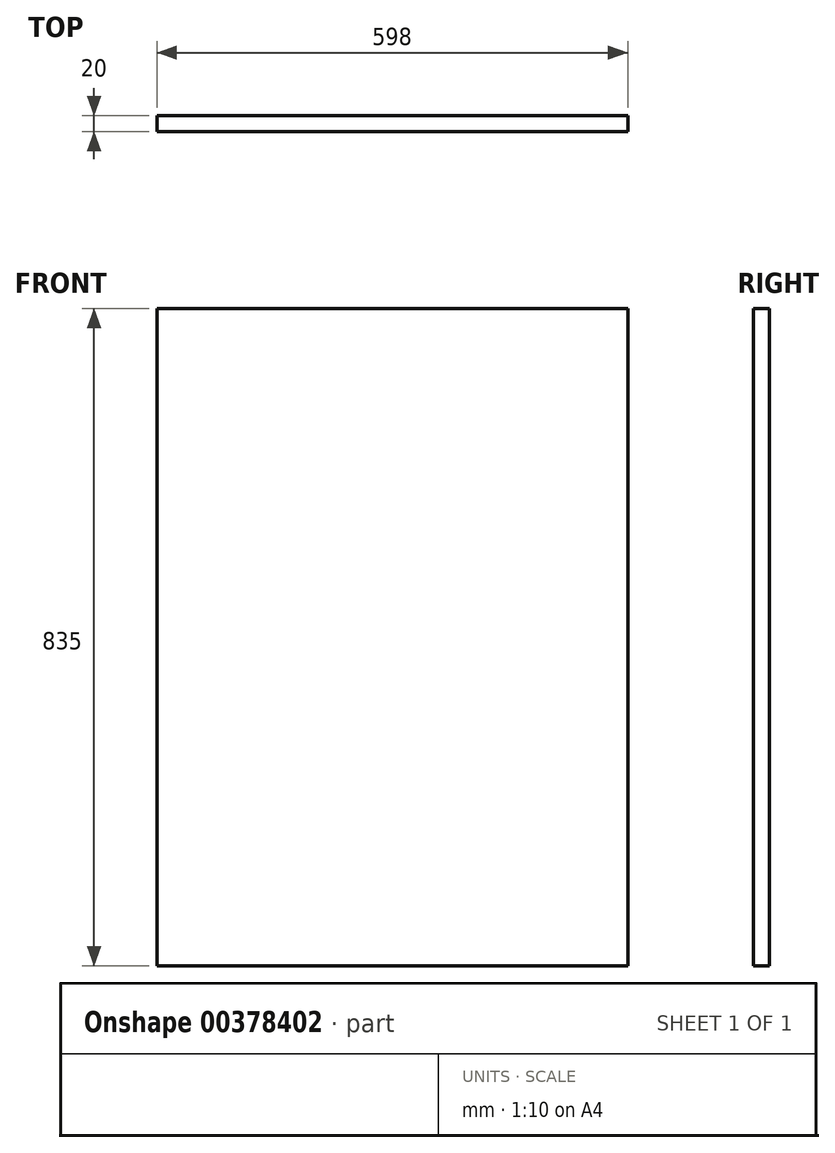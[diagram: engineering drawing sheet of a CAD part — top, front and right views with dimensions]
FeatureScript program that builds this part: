
annotation { "Feature Type Name" : "Feature", "Feature Type Description" : "" }
export const myFeature = defineFeature(function(context is Context, id is Id, definition is map)
    precondition{}
    {
        {
            var Q0;
            Q0=qCreatedBy(makeId("Front.planeOp"),FACE);
            var sketch = newSketch(context, id + "F0", { "sketchPlane" : qUnion([Q0])});
            skLineSegment(sketch, "E0.bottom", {"start": v(299, 417.5) * mm, "end": v(-299, 417.5) * mm});
            skLineSegment(sketch, "E0.top", {"start": v(299, -417.5) * mm, "end": v(-299, -417.5) * mm});
            skLineSegment(sketch, "E0.left", {"start": v(299, 417.5) * mm, "end": v(299, -417.5) * mm});
            skLineSegment(sketch, "E0.right", {"start": v(-299, 417.5) * mm, "end": v(-299, -417.5) * mm});
            skPoint(sketch, "E0.middle", {"position": v(0, 0) * mm});
            skSolve(sketch);
        }
        {
            var Q0;
            Q0 = qSketchRegion(id + "F0", true);
            extrude(context, id + "F1", {"entities" : qUnion([Q0]), "depth" : 20 * mm});
        }
    });
